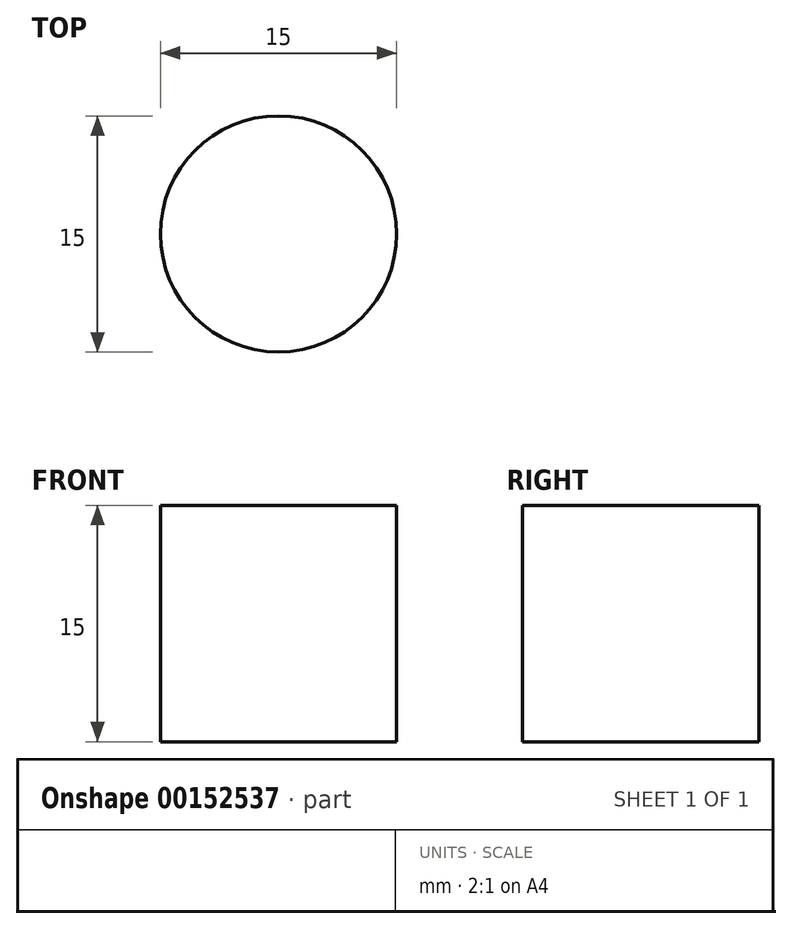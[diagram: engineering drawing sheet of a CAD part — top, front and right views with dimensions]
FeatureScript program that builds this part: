
annotation { "Feature Type Name" : "Feature", "Feature Type Description" : "" }
export const myFeature = defineFeature(function(context is Context, id is Id, definition is map)
    precondition{}
    {
        {
            var Q0;
            Q0=qCreatedBy(makeId("Top.planeOp"),FACE);
            var sketch = newSketch(context, id + "F0", { "sketchPlane" : qUnion([Q0])});
            skCircle(sketch, "E0", {"center": v(0, 0) * mm, "radius": 7.5 * mm});
            skSolve(sketch);
        }
        {
            var Q0;
            Q0=makeQuery(id+"F0.imprint","IMPRINT",FACE,{"disambiguationData":[TD([[makeQuery(id+"F0.imprint","IMPRINT",EDGE,{"derivedFrom":sQuery(id+"F0.wireOp",EDGE,"E0")}),1.0]])]});
            extrude(context, id + "F1", {"entities" : qUnion([Q0]), "depth" : 15 * mm});
        }
    });
